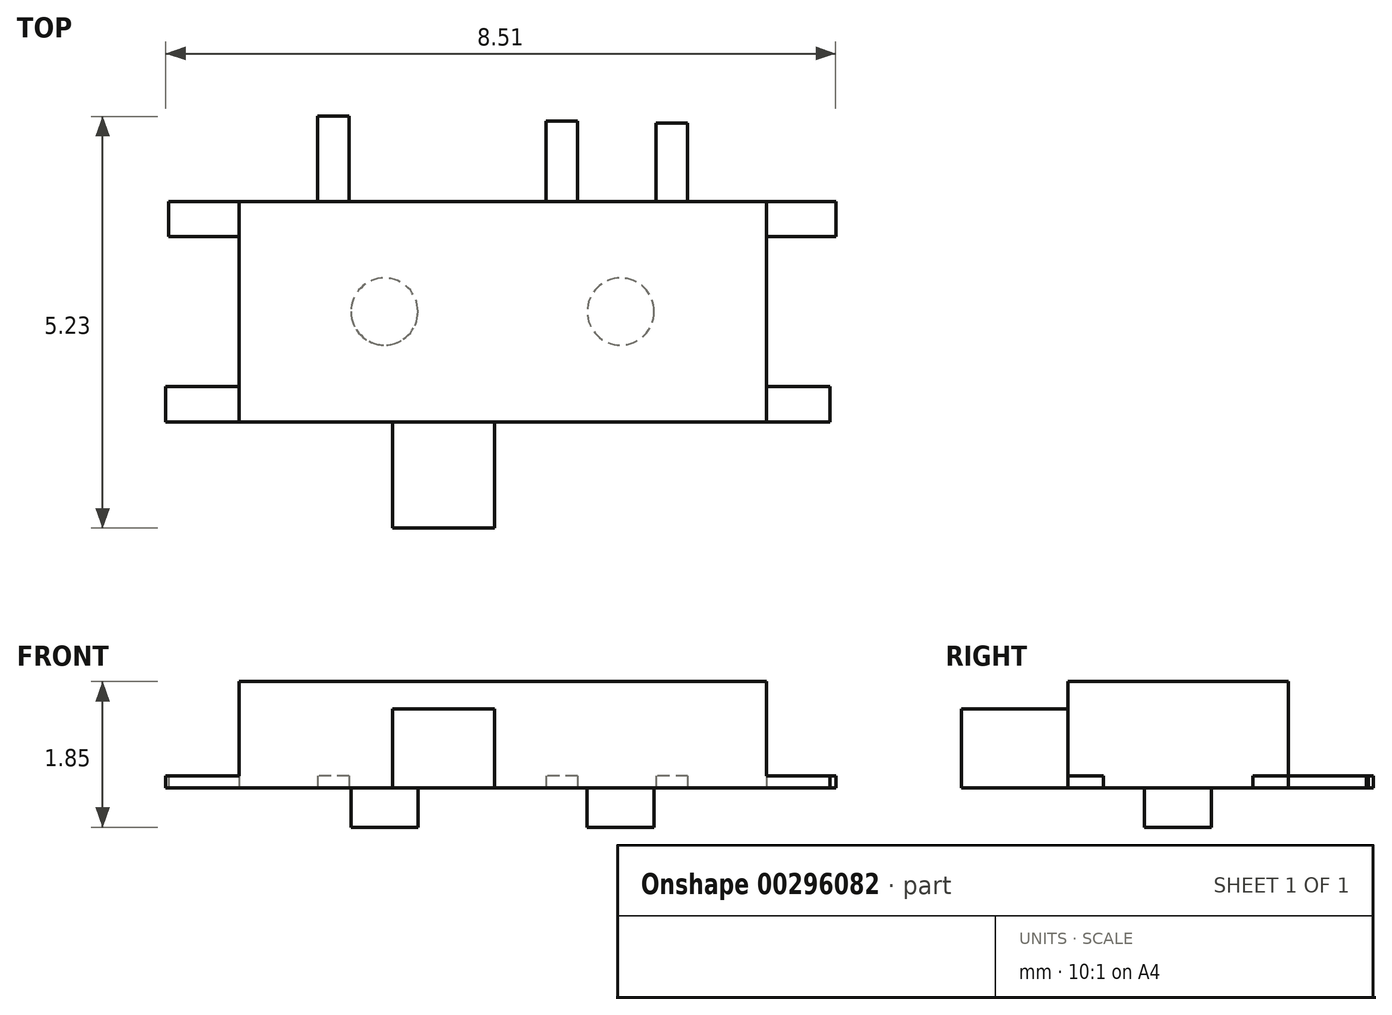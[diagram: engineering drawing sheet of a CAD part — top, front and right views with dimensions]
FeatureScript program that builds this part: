
annotation { "Feature Type Name" : "Feature", "Feature Type Description" : "" }
export const myFeature = defineFeature(function(context is Context, id is Id, definition is map)
    precondition{}
    {
        {
            var Q0;
            Q0=qCreatedBy(makeId("Top.planeOp"),FACE);
            var sketch = newSketch(context, id + "F0", { "sketchPlane" : qUnion([Q0])});
            skLineSegment(sketch, "E0.bottom", {"start": v(0, 0) * mm, "end": v(6.7, 0) * mm});
            skLineSegment(sketch, "E0.top", {"start": v(0, 2.8) * mm, "end": v(6.7, 2.8) * mm});
            skLineSegment(sketch, "E0.left", {"start": v(0, 0) * mm, "end": v(0, 2.8) * mm});
            skLineSegment(sketch, "E0.right", {"start": v(6.7, 0) * mm, "end": v(6.7, 2.8) * mm});
            skSolve(sketch);
        }
        {
            var Q0;
            Q0 = qSketchRegion(id + "F0", true);
            extrude(context, id + "F1", {"entities" : qUnion([Q0]), "depth" : 1.35 * mm});
        }
        {
            var Q0;
            Q0=qCreatedBy(makeId("Top.planeOp"),FACE);
            var sketch = newSketch(context, id + "F2", { "sketchPlane" : qUnion([Q0])});
            skLineSegment(sketch, "E1.bottom", {"start": v(5.7, 2.8) * mm, "end": v(5.3, 2.8) * mm});
            skLineSegment(sketch, "E1.top", {"start": v(5.7, 3.8) * mm, "end": v(5.3, 3.8) * mm});
            skLineSegment(sketch, "E1.left", {"start": v(5.7, 2.8) * mm, "end": v(5.7, 3.8) * mm});
            skLineSegment(sketch, "E1.right", {"start": v(5.3, 2.8) * mm, "end": v(5.3, 3.8) * mm});
            skLineSegment(sketch, "E2.bottom", {"start": v(4.3, 2.8) * mm, "end": v(3.9, 2.8) * mm});
            skLineSegment(sketch, "E2.top", {"start": v(4.3, 3.82) * mm, "end": v(3.9, 3.82) * mm});
            skLineSegment(sketch, "E2.left", {"start": v(4.3, 2.8) * mm, "end": v(4.3, 3.82) * mm});
            skLineSegment(sketch, "E2.right", {"start": v(3.9, 2.8) * mm, "end": v(3.9, 3.82) * mm});
            skLineSegment(sketch, "E3.bottom", {"start": v(1.4, 2.8) * mm, "end": v(1, 2.8) * mm});
            skLineSegment(sketch, "E3.top", {"start": v(1.4, 3.88) * mm, "end": v(1, 3.88) * mm});
            skLineSegment(sketch, "E3.left", {"start": v(1.4, 2.8) * mm, "end": v(1.4, 3.88) * mm});
            skLineSegment(sketch, "E3.right", {"start": v(1, 2.8) * mm, "end": v(1, 3.88) * mm});
            skLineSegment(sketch, "E4.bottom", {"start": v(6.7, 2.8) * mm, "end": v(7.58, 2.8) * mm});
            skLineSegment(sketch, "E4.top", {"start": v(6.7, 2.35) * mm, "end": v(7.58, 2.35) * mm});
            skLineSegment(sketch, "E4.left", {"start": v(6.7, 2.8) * mm, "end": v(6.7, 2.35) * mm});
            skLineSegment(sketch, "E4.right", {"start": v(7.58, 2.8) * mm, "end": v(7.58, 2.35) * mm});
            skLineSegment(sketch, "E5.bottom", {"start": v(6.7, 0.45) * mm, "end": v(7.5, 0.45) * mm});
            skLineSegment(sketch, "E5.top", {"start": v(6.7, 0) * mm, "end": v(7.5, 0) * mm});
            skLineSegment(sketch, "E5.left", {"start": v(6.7, 0.45) * mm, "end": v(6.7, 0) * mm});
            skLineSegment(sketch, "E5.right", {"start": v(7.5, 0.45) * mm, "end": v(7.5, 0) * mm});
            skLineSegment(sketch, "E6.bottom", {"start": v(0, 2.8) * mm, "end": v(-0.9, 2.8) * mm});
            skLineSegment(sketch, "E6.top", {"start": v(0, 2.35) * mm, "end": v(-0.9, 2.35) * mm});
            skLineSegment(sketch, "E6.left", {"start": v(0, 2.8) * mm, "end": v(0, 2.35) * mm});
            skLineSegment(sketch, "E6.right", {"start": v(-0.9, 2.8) * mm, "end": v(-0.9, 2.35) * mm});
            skLineSegment(sketch, "E7.bottom", {"start": v(0, 0.45) * mm, "end": v(-0.93, 0.45) * mm});
            skLineSegment(sketch, "E7.top", {"start": v(0, 0) * mm, "end": v(-0.93, 0) * mm});
            skLineSegment(sketch, "E7.left", {"start": v(0, 0.45) * mm, "end": v(0, 0) * mm});
            skLineSegment(sketch, "E7.right", {"start": v(-0.93, 0.45) * mm, "end": v(-0.93, 0) * mm});
            skSolve(sketch);
        }
        {
            var Q0;
            Q0 = qSketchRegion(id + "F2", true);
            extrude(context, id + "F3", {"entities" : qUnion([Q0]), "operationType" : NewBodyOperationType.ADD, "depth" : 0.15 * mm});
        }
        {
            var Q0;
            Q0=qCreatedBy(makeId("Top.planeOp"),FACE);
            var sketch = newSketch(context, id + "F4", { "sketchPlane" : qUnion([Q0])});
            skLineSegment(sketch, "E8.bottom", {"start": v(1.95, 0) * mm, "end": v(3.25, 0) * mm});
            skLineSegment(sketch, "E8.top", {"start": v(1.95, -1.35) * mm, "end": v(3.25, -1.35) * mm});
            skLineSegment(sketch, "E8.left", {"start": v(1.95, 0) * mm, "end": v(1.95, -1.35) * mm});
            skLineSegment(sketch, "E8.right", {"start": v(3.25, 0) * mm, "end": v(3.25, -1.35) * mm});
            skSolve(sketch);
        }
        {
            var Q0;
            Q0 = qSketchRegion(id + "F4", true);
            extrude(context, id + "F5", {"entities" : qUnion([Q0]), "operationType" : NewBodyOperationType.ADD, "depth" : 1 * mm});
        }
        {
            var Q0;
            Q0=makeQuery(id+"F5.boolean.opBoolean","MERGE",FACE,{"derivedFrom":[makeQuery(id+"F3.boolean.opBoolean","MERGE",FACE,{"derivedFrom":[makeQuery(id+"F1.opExtrude","CAP_FACE",FACE,{"disambiguationData":[OSD([sQuery(id+"F0.wireOp",EDGE,"E0.bottom"),sQuery(id+"F0.wireOp",EDGE,"E0.top"),sQuery(id+"F0.wireOp",EDGE,"E0.left"),sQuery(id+"F0.wireOp",EDGE,"E0.right")])],"isStart":true}),makeQuery(id+"F3.opExtrude","CAP_FACE",FACE,{"disambiguationData":[OSD([sQuery(id+"F2.wireOp",EDGE,"E1.bottom"),sQuery(id+"F2.wireOp",EDGE,"E1.top"),sQuery(id+"F2.wireOp",EDGE,"E1.left"),sQuery(id+"F2.wireOp",EDGE,"E1.right")])],"isStart":true}),makeQuery(id+"F3.opExtrude","CAP_FACE",FACE,{"disambiguationData":[OSD([sQuery(id+"F2.wireOp",EDGE,"E2.bottom"),sQuery(id+"F2.wireOp",EDGE,"E2.top"),sQuery(id+"F2.wireOp",EDGE,"E2.left"),sQuery(id+"F2.wireOp",EDGE,"E2.right")])],"isStart":true}),makeQuery(id+"F3.opExtrude","CAP_FACE",FACE,{"disambiguationData":[OSD([sQuery(id+"F2.wireOp",EDGE,"E3.bottom"),sQuery(id+"F2.wireOp",EDGE,"E3.top"),sQuery(id+"F2.wireOp",EDGE,"E3.left"),sQuery(id+"F2.wireOp",EDGE,"E3.right")])],"isStart":true}),makeQuery(id+"F3.opExtrude","CAP_FACE",FACE,{"disambiguationData":[OSD([sQuery(id+"F2.wireOp",EDGE,"E4.bottom"),sQuery(id+"F2.wireOp",EDGE,"E4.top"),sQuery(id+"F2.wireOp",EDGE,"E4.left"),sQuery(id+"F2.wireOp",EDGE,"E4.right")])],"isStart":true}),makeQuery(id+"F3.opExtrude","CAP_FACE",FACE,{"disambiguationData":[OSD([sQuery(id+"F2.wireOp",EDGE,"E5.bottom"),sQuery(id+"F2.wireOp",EDGE,"E5.top"),sQuery(id+"F2.wireOp",EDGE,"E5.left"),sQuery(id+"F2.wireOp",EDGE,"E5.right")])],"isStart":true}),makeQuery(id+"F3.opExtrude","CAP_FACE",FACE,{"disambiguationData":[OSD([sQuery(id+"F2.wireOp",EDGE,"E6.bottom"),sQuery(id+"F2.wireOp",EDGE,"E6.top"),sQuery(id+"F2.wireOp",EDGE,"E6.left"),sQuery(id+"F2.wireOp",EDGE,"E6.right")])],"isStart":true}),makeQuery(id+"F3.opExtrude","CAP_FACE",FACE,{"disambiguationData":[OSD([sQuery(id+"F2.wireOp",EDGE,"E7.bottom"),sQuery(id+"F2.wireOp",EDGE,"E7.top"),sQuery(id+"F2.wireOp",EDGE,"E7.left"),sQuery(id+"F2.wireOp",EDGE,"E7.right")])],"isStart":true})]}),makeQuery(id+"F5.opExtrude","CAP_FACE",FACE,{"disambiguationData":[OSD([sQuery(id+"F4.wireOp",EDGE,"E8.bottom"),sQuery(id+"F4.wireOp",EDGE,"E8.top"),sQuery(id+"F4.wireOp",EDGE,"E8.left"),sQuery(id+"F4.wireOp",EDGE,"E8.right")])],"isStart":true})]});
            var sketch = newSketch(context, id + "F6", { "sketchPlane" : qUnion([Q0])});
            skCircle(sketch, "E9", {"center": v(4.85, -1.4) * mm, "radius": 0.42 * mm});
            skCircle(sketch, "E10", {"center": v(1.85, -1.4) * mm, "radius": 0.42 * mm});
            skLineSegment(sketch, "E11", {"start": v(1.85, -1.4) * mm, "end": v(4.85, -1.4) * mm, "construction": true});
            skSolve(sketch);
        }
        {
            var Q0;
            Q0 = qSketchRegion(id + "F6", true);
            extrude(context, id + "F7", {"entities" : qUnion([Q0]), "operationType" : NewBodyOperationType.ADD, "depth" : 0.5 * mm});
        }
    });
